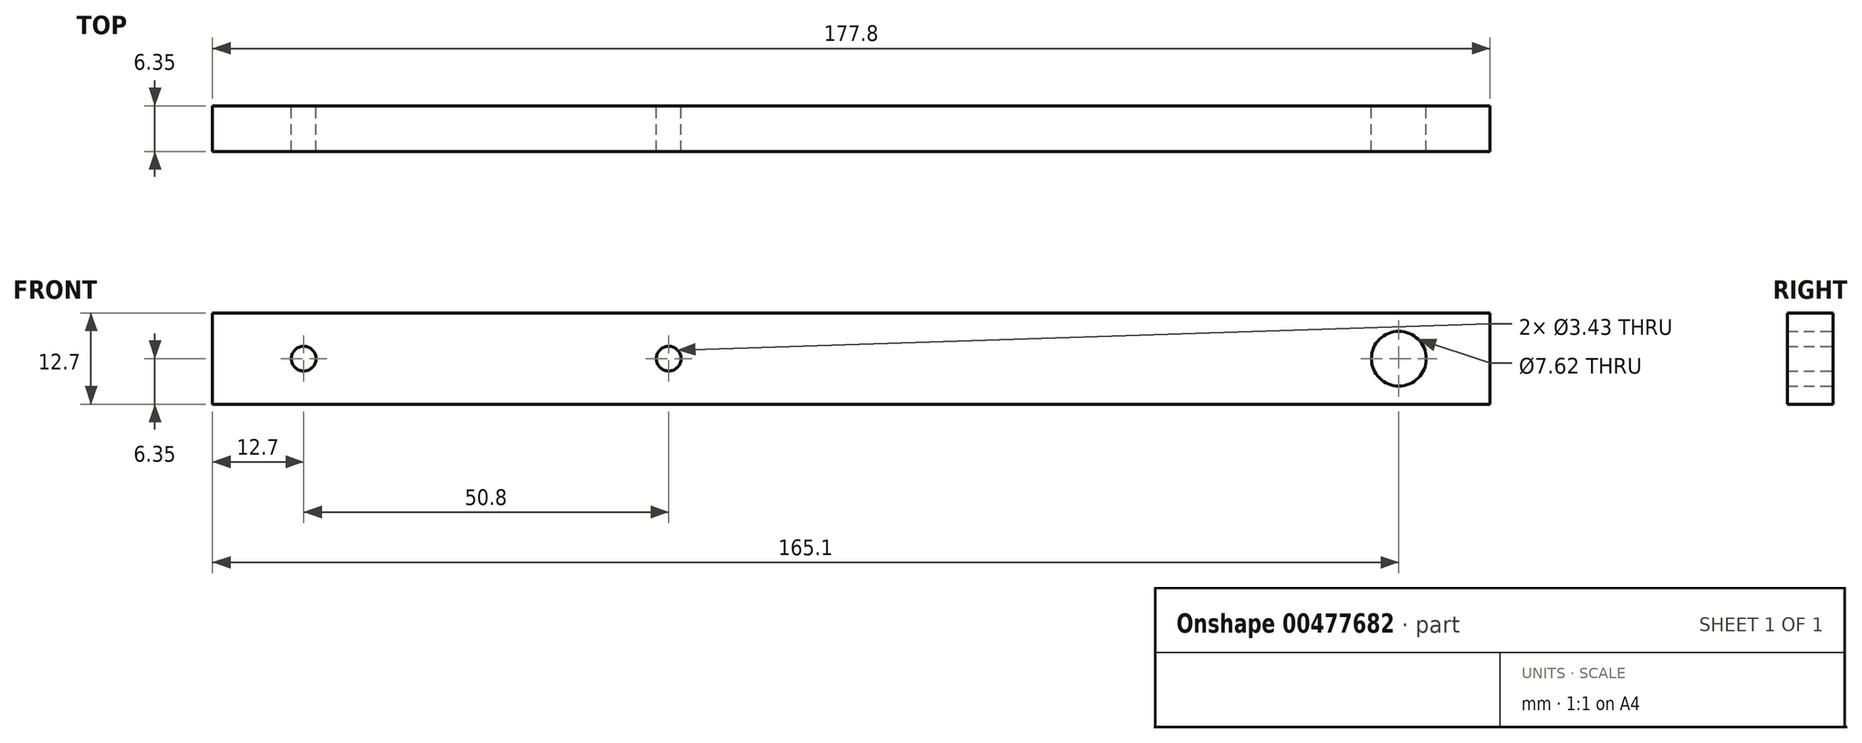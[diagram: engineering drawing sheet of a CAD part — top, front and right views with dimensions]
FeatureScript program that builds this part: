
annotation { "Feature Type Name" : "Feature", "Feature Type Description" : "" }
export const myFeature = defineFeature(function(context is Context, id is Id, definition is map)
    precondition{}
    {
        {
            var Q0;
            Q0=qCreatedBy(makeId("Front.planeOp"),FACE);
            var sketch = newSketch(context, id + "F0", { "sketchPlane" : qUnion([Q0])});
            skLineSegment(sketch, "E0.bottom", {"start": v(-88.9, 6.35) * mm, "end": v(88.9, 6.35) * mm});
            skLineSegment(sketch, "E0.top", {"start": v(-88.9, -6.35) * mm, "end": v(88.9, -6.35) * mm});
            skLineSegment(sketch, "E0.left", {"start": v(-88.9, 6.35) * mm, "end": v(-88.9, -6.35) * mm});
            skLineSegment(sketch, "E0.right", {"start": v(88.9, 6.35) * mm, "end": v(88.9, -6.35) * mm});
            skPoint(sketch, "E0.middle", {"position": v(0, 0) * mm});
            skPoint(sketch, "E1", {"position": v(-76.2, 0) * mm});
            skPoint(sketch, "E2", {"position": v(-25.4, 0) * mm});
            skCircle(sketch, "E3", {"center": v(76.2, 0) * mm, "radius": 3.81 * mm});
            skCircle(sketch, "E4", {"center": v(-25.4, 0) * mm, "radius": 1.27 * mm});
            skCircle(sketch, "E5", {"center": v(-76.2, 0) * mm, "radius": 1.27 * mm});
            skSolve(sketch);
        }
        {
            var Q0;
            Q0=makeQuery(id+"F0.imprint","IMPRINT",FACE,{"disambiguationData":[TD([[makeQuery(id+"F0.imprint","IMPRINT",EDGE,{"derivedFrom":sQuery(id+"F0.wireOp",EDGE,"E3")}),1.0]])]});
            extrude(context, id + "F1", {"entities" : qUnion([Q0]), "depth" : 25.4 * mm, "offsetDistance" : 25.4 * mm});
        }
        {
            var Q0;
            Q0 = qSketchRegion(id + "F0", true);
            var Q1;
            Q1=makeQuery(id+"F0.imprint","IMPRINT",FACE,{"disambiguationData":[TD([[makeQuery(id+"F0.imprint","IMPRINT",EDGE,{"derivedFrom":sQuery(id+"F0.wireOp",EDGE,"E4")}),1.0]])]});
            var Q2;
            Q2=makeQuery(id+"F0.imprint","IMPRINT",FACE,{"disambiguationData":[TD([[makeQuery(id+"F0.imprint","IMPRINT",EDGE,{"derivedFrom":sQuery(id+"F0.wireOp",EDGE,"E5")}),1.0]])]});
            extrude(context, id + "F2", {"entities" : qUnion([Q0, Q1, Q2]), "operationType" : NewBodyOperationType.ADD, "depth" : 6.35 * mm, "offsetDistance" : 25.4 * mm});
        }
        {
            var Q0;
            Q0=sQuery(id+"F0.wireOp",VERTEX,"E2");
            var Q1;
            Q1=sQuery(id+"F0.wireOp",VERTEX,"E1");
            var Q2;
            Q2=makeQuery(id+"F1.opExtrude","SWEPT_BODY",BODY,{"disambiguationData":[OSD([sQuery(id+"F0.wireOp",EDGE,"E3")])]});
            hole(context, id + "F3", {"style" : HoleStyle.SIMPLE, "endStyle" : HoleEndStyle.THROUGH, "oppositeDirection" : true, "holeDiameter" : 3.43 * mm, "majorDiameter" : 6.35 * mm, "isTappedThrough" : true, "tappedDepth" : 12.7 * mm, "tapClearance" : 3, "locations" : qUnion([Q0, Q1]), "scope" : qUnion([Q2])});
        }
        {
            var Q0;
            Q0=sQuery(id+"F0.wireOp",VERTEX,"E3.center");
            var Q1;
            Q1=makeQuery(id+"F1.opExtrude","SWEPT_BODY",BODY,{"disambiguationData":[OSD([sQuery(id+"F0.wireOp",EDGE,"E3")])]});
            hole(context, id + "F4", {"style" : HoleStyle.SIMPLE, "endStyle" : HoleEndStyle.THROUGH, "oppositeDirection" : true, "holeDiameter" : 7.62 * mm, "majorDiameter" : 6.35 * mm, "isTappedThrough" : true, "tappedDepth" : 12.7 * mm, "tapClearance" : 3, "locations" : qUnion([Q0]), "scope" : qUnion([Q1])});
        }
    });
